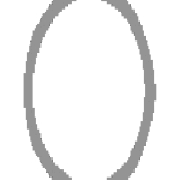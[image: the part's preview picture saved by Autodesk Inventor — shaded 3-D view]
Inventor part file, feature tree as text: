
AUTODESK INVENTOR PART (.ipt)
format: ipt  version: 2021 (Build 250183000, 183)  size: 112,640 bytes
history: native  units: in
note: dims shown in document units (in); Inventor stores cm internally (conversion verified against a paired STEP export)
features: other x4, sketch x3, plane x1
ambient origin geometry x8: Origin, YZ Plane, XZ Plane, XY Plane, X Axis, Y Axis, Z Axis, Center Point
bodies: Solid1 (feature_tree), Body (feature_tree)
feature tree (8):
  other  "Driven Length"
  other  "Frame Generator"
  other  "Start Plane"
  other  "End Plane"
  sketch  "Sketch"  dims[d2=15.625in d4=-0.0in d5=15.625in d6=0.12in d7=0.0in d8=90.0deg d9=15.625in]
  sketch  "Sketch2"  dims[d0=1.0in]
  plane  "Work Plane3"
  sketch  "Sketch3"  dims[d1=0.065in]
